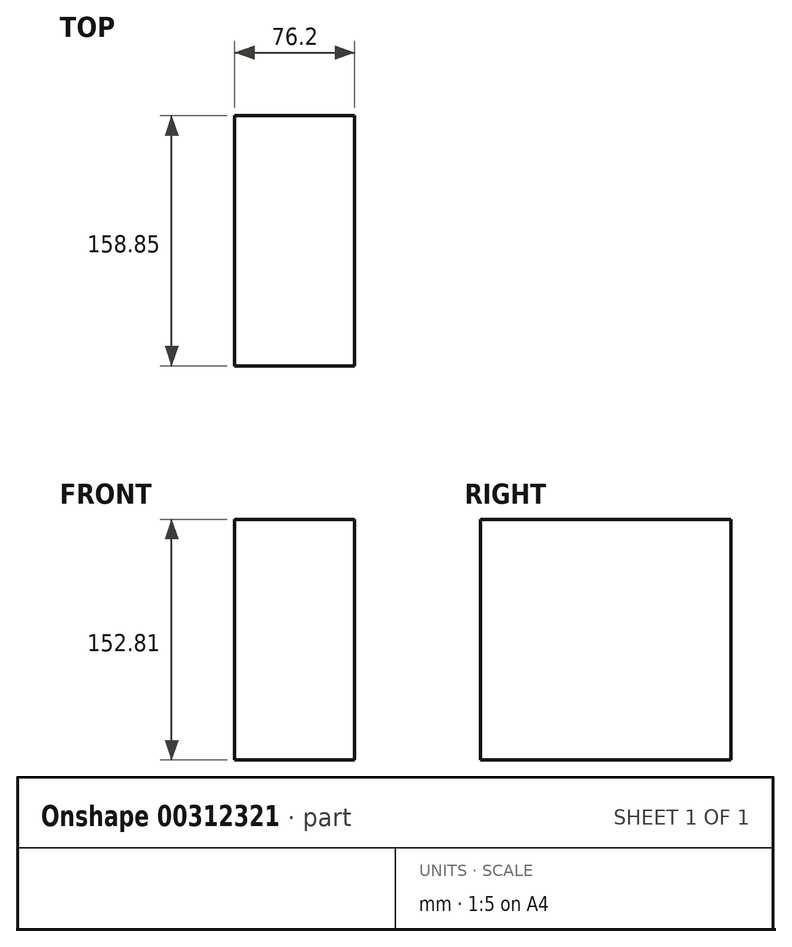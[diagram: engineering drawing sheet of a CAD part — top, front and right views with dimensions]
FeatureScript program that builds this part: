
annotation { "Feature Type Name" : "Feature", "Feature Type Description" : "" }
export const myFeature = defineFeature(function(context is Context, id is Id, definition is map)
    precondition{}
    {
        {
            var Q0;
            Q0=qCreatedBy(makeId("Right.planeOp"),FACE);
            var sketch = newSketch(context, id + "F0", { "sketchPlane" : qUnion([Q0])});
            skLineSegment(sketch, "E0.bottom", {"start": v(-80.11, 77.04) * mm, "end": v(78.74, 77.04) * mm});
            skLineSegment(sketch, "E0.top", {"start": v(-80.11, -75.77) * mm, "end": v(78.74, -75.77) * mm});
            skLineSegment(sketch, "E0.left", {"start": v(-80.11, 77.04) * mm, "end": v(-80.11, -75.77) * mm});
            skLineSegment(sketch, "E0.right", {"start": v(78.74, 77.04) * mm, "end": v(78.74, -75.77) * mm});
            skSolve(sketch);
        }
        {
            var Q0;
            Q0 = qSketchRegion(id + "F0", true);
            extrude(context, id + "F1", {"entities" : qUnion([Q0]), "depth" : 76.2 * mm});
        }
    });
